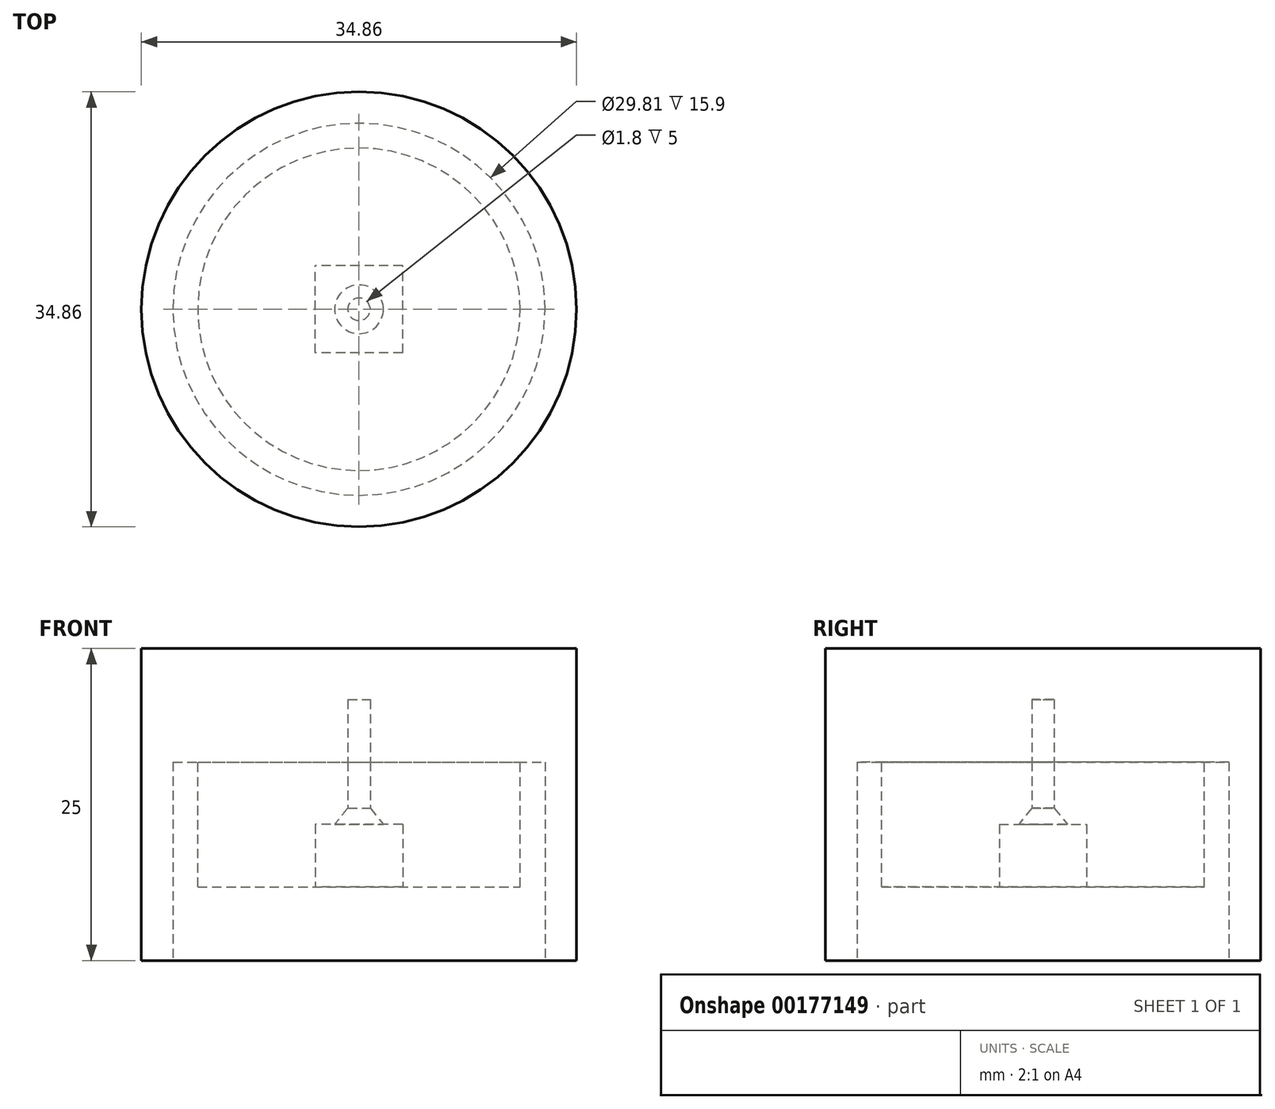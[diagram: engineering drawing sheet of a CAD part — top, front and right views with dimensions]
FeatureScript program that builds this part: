
annotation { "Feature Type Name" : "Feature", "Feature Type Description" : "" }
export const myFeature = defineFeature(function(context is Context, id is Id, definition is map)
    precondition{}
    {
        {
            var Q0;
            Q0=qCreatedBy(makeId("Top.planeOp"),FACE);
            var sketch = newSketch(context, id + "F0", { "sketchPlane" : qUnion([Q0])});
            skCircle(sketch, "E0", {"center": v(0, 0) * mm, "radius": 17.43 * mm});
            skSolve(sketch);
        }
        {
            var Q0;
            Q0 = qSketchRegion(id + "F0", true);
            extrude(context, id + "F1", {"entities" : qUnion([Q0]), "depth" : 25 * mm});
        }
        {
            var Q0;
            Q0=makeQuery(id+"F1.opExtrude","CAP_FACE",FACE,{"disambiguationData":[OSD([sQuery(id+"F0.wireOp",EDGE,"E0")])],"isStart":true});
            var sketch = newSketch(context, id + "F2", { "sketchPlane" : qUnion([Q0])});
            skCircle(sketch, "E1", {"center": v(0, 0) * mm, "radius": 14.9 * mm});
            skSolve(sketch);
        }
        {
            var Q0;
            Q0 = qSketchRegion(id + "F2", true);
            extrude(context, id + "F3", {"entities" : qUnion([Q0]), "operationType" : NewBodyOperationType.REMOVE, "oppositeDirection" : true, "depth" : 15.9 * mm});
        }
        {
            var Q0;
            Q0=makeQuery(id+"F3.boolean.opBoolean","COPY",FACE,{"derivedFrom":makeQuery(id+"F3.opExtrude","CAP_FACE",FACE,{"disambiguationData":[OSD([sQuery(id+"F2.wireOp",EDGE,"E1")])],"isStart":false})});
            var sketch = newSketch(context, id + "F4", { "sketchPlane" : qUnion([Q0])});
            skCircle(sketch, "E2", {"center": v(0, 0) * mm, "radius": 0.9 * mm});
            skSolve(sketch);
        }
        {
            var Q0;
            Q0 = qSketchRegion(id + "F4", true);
            extrude(context, id + "F5", {"entities" : qUnion([Q0]), "operationType" : NewBodyOperationType.REMOVE, "oppositeDirection" : true, "depth" : 5 * mm});
        }
        {
            var Q0;
            Q0=makeQuery(id+"F3.boolean.opBoolean","COPY",FACE,{"derivedFrom":makeQuery(id+"F3.opExtrude","CAP_FACE",FACE,{"disambiguationData":[OSD([sQuery(id+"F2.wireOp",EDGE,"E1")])],"isStart":false})});
            var sketch = newSketch(context, id + "F6", { "sketchPlane" : qUnion([Q0])});
            skCircle(sketch, "E3", {"center": v(0, 0) * mm, "radius": 12.92 * mm});
            skSolve(sketch);
        }
        {
            var Q0;
            Q0 = qSketchRegion(id + "F6", true);
            extrude(context, id + "F7", {"entities" : qUnion([Q0]), "depth" : 10 * mm});
        }
        {
            var Q0;
            Q0=makeQuery(id+"F7.opExtrude","CAP_FACE",FACE,{"disambiguationData":[OSD([sQuery(id+"F6.wireOp",EDGE,"E3")])],"isStart":false});
            var sketch = newSketch(context, id + "F8", { "sketchPlane" : qUnion([Q0])});
            skCircle(sketch, "E4", {"center": v(0, 0) * mm, "radius": 1.34 * mm});
            skSolve(sketch);
        }
        {
            var Q0;
            Q0=makeQuery(id+"F8.imprint","IMPRINT",FACE,{"disambiguationData":[TD([[makeQuery(id+"F8.imprint","IMPRINT",EDGE,{"derivedFrom":sQuery(id+"F8.wireOp",EDGE,"E4")}),-1.0]])]});
            var sketch = newSketch(context, id + "F9", { "sketchPlane" : qUnion([Q0])});
            skLineSegment(sketch, "E5.bottom", {"start": v(3.5, 3.5) * mm, "end": v(-3.5, 3.5) * mm});
            skLineSegment(sketch, "E5.top", {"start": v(3.5, -3.5) * mm, "end": v(-3.5, -3.5) * mm});
            skLineSegment(sketch, "E5.left", {"start": v(3.5, 3.5) * mm, "end": v(3.5, -3.5) * mm});
            skLineSegment(sketch, "E5.right", {"start": v(-3.5, 3.5) * mm, "end": v(-3.5, -3.5) * mm});
            skPoint(sketch, "E5.middle", {"position": v(0, 0) * mm});
            skSolve(sketch);
        }
        {
            var Q0;
            Q0 = qSketchRegion(id + "F9", true);
            extrude(context, id + "F10", {"entities" : qUnion([Q0]), "operationType" : NewBodyOperationType.REMOVE, "oppositeDirection" : true, "depth" : 5 * mm});
        }
        {
            var Q0;
            Q0=sQuery(id+"F8.wireOp",VERTEX,"E4.center");
            var Q1;
            Q1=makeQuery(id+"F7.opExtrude","SWEPT_BODY",BODY,{"disambiguationData":[OSD([sQuery(id+"F6.wireOp",EDGE,"E3")])]});
            hole(context, id + "F11", {"style" : HoleStyle.C_SINK, "endStyle" : HoleEndStyle.BLIND, "holeDiameter" : 1.8 * mm, "cSinkDiameter" : 3.9 * mm, "cSinkAngle" : 76.73 * degree, "holeDepth" : 5 * mm, "tappedDepth" : 12 * mm, "tapClearance" : 3, "locations" : qUnion([Q0]), "scope" : qUnion([Q1])});
        }
    });
